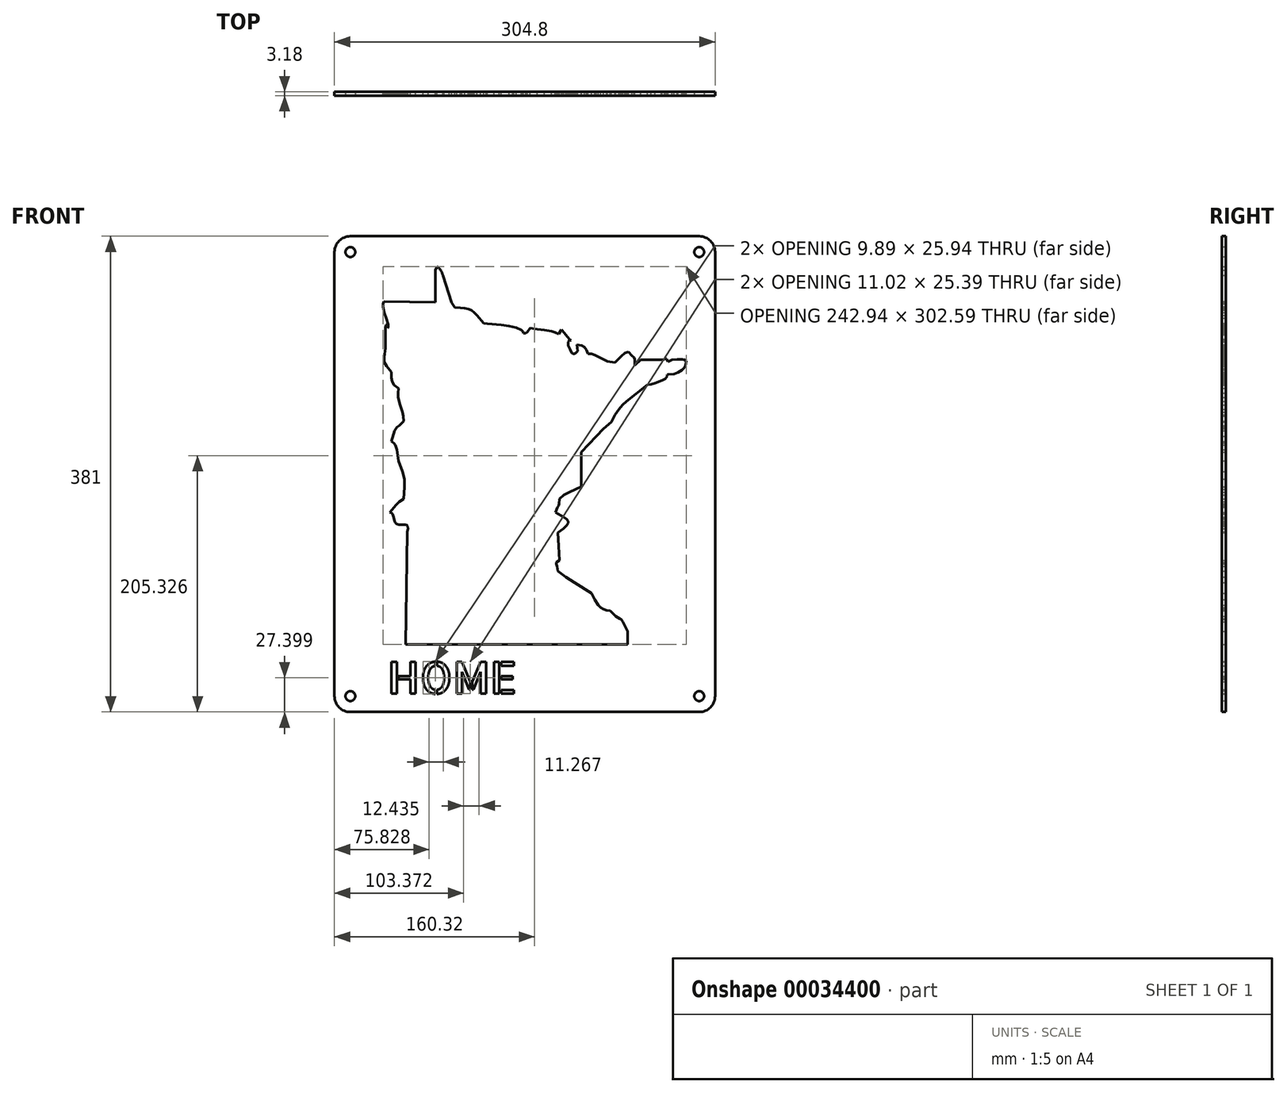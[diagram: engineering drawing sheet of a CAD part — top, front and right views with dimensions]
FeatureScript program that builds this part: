
annotation { "Feature Type Name" : "Feature", "Feature Type Description" : "" }
export const myFeature = defineFeature(function(context is Context, id is Id, definition is map)
    precondition{}
    {
        {
            var Q0;
            Q0=qCreatedBy(makeId("Front.planeOp"),FACE);
            var sketch = newSketch(context, id + "F0", { "sketchPlane" : qUnion([Q0])});
            skLineSegment(sketch, "E0", {"start": v(-79.4, 123.25) * mm, "end": v(-120.64, 123.97) * mm});
            skLineSegment(sketch, "E1", {"start": v(-120.64, 123.97) * mm, "end": v(-121.3, 121.8) * mm});
            skLineSegment(sketch, "E2", {"start": v(-121.3, 121.8) * mm, "end": v(-121.47, 119.63) * mm});
            skLineSegment(sketch, "E3", {"start": v(-121.47, 119.63) * mm, "end": v(-120.55, 115.04) * mm});
            skLineSegment(sketch, "E4", {"start": v(-120.55, 115.04) * mm, "end": v(-118.8, 110.36) * mm});
            skLineSegment(sketch, "E5", {"start": v(-118.8, 110.36) * mm, "end": v(-117.21, 105.52) * mm});
            skLineSegment(sketch, "E6", {"start": v(-117.21, 105.52) * mm, "end": v(-117.3, 102.76) * mm});
            skLineSegment(sketch, "E7", {"start": v(-117.3, 102.76) * mm, "end": v(-117.63, 102.51) * mm});
            skLineSegment(sketch, "E8", {"start": v(-117.63, 102.51) * mm, "end": v(-118.63, 104.85) * mm});
            skLineSegment(sketch, "E9", {"start": v(-118.63, 104.85) * mm, "end": v(-118.88, 105.18) * mm});
            skLineSegment(sketch, "E10", {"start": v(-118.88, 105.18) * mm, "end": v(-119.13, 105.02) * mm});
            skLineSegment(sketch, "E11", {"start": v(-119.13, 105.02) * mm, "end": v(-119.47, 102.84) * mm});
            skLineSegment(sketch, "E12", {"start": v(-119.47, 102.84) * mm, "end": v(-119.55, 86.3) * mm});
            skLineSegment(sketch, "E13", {"start": v(-119.55, 86.3) * mm, "end": v(-120.47, 79.38) * mm});
            skLineSegment(sketch, "E14", {"start": v(-120.47, 79.38) * mm, "end": v(-120.47, 75.28) * mm});
            skLineSegment(sketch, "E15", {"start": v(-120.47, 75.28) * mm, "end": v(-118.71, 72.03) * mm});
            skLineSegment(sketch, "E16", {"start": v(-118.71, 72.03) * mm, "end": v(-114.87, 67.18) * mm});
            skLineSegment(sketch, "E17", {"start": v(-114.87, 67.18) * mm, "end": v(-114.79, 62.84) * mm});
            skLineSegment(sketch, "E18", {"start": v(-114.79, 62.84) * mm, "end": v(-114.2, 59.58) * mm});
            skLineSegment(sketch, "E19", {"start": v(-114.2, 59.58) * mm, "end": v(-112.45, 56.91) * mm});
            skLineSegment(sketch, "E20", {"start": v(-112.45, 56.91) * mm, "end": v(-109.03, 54.4) * mm});
            skLineSegment(sketch, "E21", {"start": v(-109.03, 54.4) * mm, "end": v(-109.44, 50.56) * mm});
            skLineSegment(sketch, "E22", {"start": v(-109.44, 50.56) * mm, "end": v(-109.28, 47.14) * mm});
            skLineSegment(sketch, "E23", {"start": v(-109.28, 47.14) * mm, "end": v(-107.77, 41.13) * mm});
            skLineSegment(sketch, "E24", {"start": v(-107.77, 41.13) * mm, "end": v(-105.77, 35.28) * mm});
            skLineSegment(sketch, "E25", {"start": v(-105.77, 35.28) * mm, "end": v(-105.1, 31.94) * mm});
            skLineSegment(sketch, "E26", {"start": v(-105.1, 31.94) * mm, "end": v(-104.85, 28.1) * mm});
            skLineSegment(sketch, "E27", {"start": v(-104.85, 28.1) * mm, "end": v(-108.53, 24.6) * mm});
            skLineSegment(sketch, "E28", {"start": v(-108.53, 24.6) * mm, "end": v(-110.45, 23.34) * mm});
            skLineSegment(sketch, "E29", {"start": v(-110.45, 23.34) * mm, "end": v(-112.12, 20.5) * mm});
            skLineSegment(sketch, "E30", {"start": v(-112.12, 20.5) * mm, "end": v(-114.87, 11.81) * mm});
            skLineSegment(sketch, "E31", {"start": v(-114.87, 11.81) * mm, "end": v(-112.95, 10.65) * mm});
            skLineSegment(sketch, "E32", {"start": v(-112.95, 10.65) * mm, "end": v(-111.7, 9.06) * mm});
            skLineSegment(sketch, "E33", {"start": v(-111.7, 9.06) * mm, "end": v(-110.36, 5.22) * mm});
            skLineSegment(sketch, "E34", {"start": v(-110.36, 5.22) * mm, "end": v(-109.03, -3.89) * mm});
            skLineSegment(sketch, "E35", {"start": v(-109.03, -3.89) * mm, "end": v(-105.77, -12.24) * mm});
            skLineSegment(sketch, "E36", {"start": v(-105.77, -12.24) * mm, "end": v(-104.35, -18.25) * mm});
            skLineSegment(sketch, "E37", {"start": v(-104.35, -18.25) * mm, "end": v(-104.18, -24.6) * mm});
            skLineSegment(sketch, "E38", {"start": v(-104.18, -24.6) * mm, "end": v(-104.85, -34.37) * mm});
            skLineSegment(sketch, "E39", {"start": v(-104.85, -34.37) * mm, "end": v(-108.28, -36.62) * mm});
            skLineSegment(sketch, "E40", {"start": v(-108.28, -36.62) * mm, "end": v(-111.03, -38.96) * mm});
            skLineSegment(sketch, "E41", {"start": v(-111.03, -38.96) * mm, "end": v(-116.04, -45.06) * mm});
            skLineSegment(sketch, "E42", {"start": v(-116.04, -45.06) * mm, "end": v(-114.7, -45.4) * mm});
            skLineSegment(sketch, "E43", {"start": v(-114.7, -45.4) * mm, "end": v(-113.87, -46.31) * mm});
            skLineSegment(sketch, "E44", {"start": v(-113.87, -46.31) * mm, "end": v(-112.95, -49.15) * mm});
            skLineSegment(sketch, "E45", {"start": v(-112.95, -49.15) * mm, "end": v(-112.2, -52.16) * mm});
            skLineSegment(sketch, "E46", {"start": v(-112.2, -52.16) * mm, "end": v(-111.62, -53.4) * mm});
            skLineSegment(sketch, "E47", {"start": v(-111.62, -53.4) * mm, "end": v(-110.78, -54.24) * mm});
            skLineSegment(sketch, "E48", {"start": v(-110.78, -54.24) * mm, "end": v(-108.78, -54.75) * mm});
            skLineSegment(sketch, "E49", {"start": v(-108.78, -54.75) * mm, "end": v(-106.86, -54.91) * mm});
            skLineSegment(sketch, "E50", {"start": v(-106.86, -54.91) * mm, "end": v(-103.68, -55) * mm});
            skLineSegment(sketch, "E51", {"start": v(-103.68, -55) * mm, "end": v(-102.51, -55.33) * mm});
            skLineSegment(sketch, "E52", {"start": v(-102.51, -55.33) * mm, "end": v(-101.76, -56.25) * mm});
            skLineSegment(sketch, "E53", {"start": v(-101.76, -56.25) * mm, "end": v(-101.51, -57.92) * mm});
            skLineSegment(sketch, "E54", {"start": v(-101.51, -57.92) * mm, "end": v(-101.93, -60.68) * mm});
            skLineSegment(sketch, "E55", {"start": v(-101.93, -60.68) * mm, "end": v(-103.35, -150.79) * mm});
            skLineSegment(sketch, "E56", {"start": v(-103.35, -150.79) * mm, "end": v(74.45, -150.87) * mm});
            skLineSegment(sketch, "E57", {"start": v(74.45, -150.87) * mm, "end": v(74.45, -140.18) * mm});
            skLineSegment(sketch, "E58", {"start": v(74.45, -140.18) * mm, "end": v(70.7, -132.66) * mm});
            skLineSegment(sketch, "E59", {"start": v(70.7, -132.66) * mm, "end": v(69.36, -130.9) * mm});
            skLineSegment(sketch, "E60", {"start": v(69.36, -130.9) * mm, "end": v(68.02, -130) * mm});
            skLineSegment(sketch, "E61", {"start": v(68.02, -130) * mm, "end": v(65.02, -128.32) * mm});
            skLineSegment(sketch, "E62", {"start": v(65.02, -128.32) * mm, "end": v(60.34, -123.9) * mm});
            skLineSegment(sketch, "E63", {"start": v(60.34, -123.9) * mm, "end": v(57.5, -123.56) * mm});
            skLineSegment(sketch, "E64", {"start": v(57.5, -123.56) * mm, "end": v(55, -122.64) * mm});
            skLineSegment(sketch, "E65", {"start": v(55, -122.64) * mm, "end": v(52.82, -121.3) * mm});
            skLineSegment(sketch, "E66", {"start": v(52.82, -121.3) * mm, "end": v(50.98, -119.47) * mm});
            skLineSegment(sketch, "E67", {"start": v(50.98, -119.47) * mm, "end": v(48.06, -114.88) * mm});
            skLineSegment(sketch, "E68", {"start": v(48.06, -114.88) * mm, "end": v(45.64, -109.7) * mm});
            skLineSegment(sketch, "E69", {"start": v(45.64, -109.7) * mm, "end": v(31.78, -101.26) * mm});
            skLineSegment(sketch, "E70", {"start": v(31.78, -101.26) * mm, "end": v(24.85, -96.75) * mm});
            skLineSegment(sketch, "E71", {"start": v(24.85, -96.75) * mm, "end": v(18.58, -91.9) * mm});
            skLineSegment(sketch, "E72", {"start": v(18.58, -91.9) * mm, "end": v(18, -88.23) * mm});
            skLineSegment(sketch, "E73", {"start": v(18, -88.23) * mm, "end": v(17.16, -86.31) * mm});
            skLineSegment(sketch, "E74", {"start": v(17.16, -86.31) * mm, "end": v(17.33, -85.06) * mm});
            skLineSegment(sketch, "E75", {"start": v(17.33, -85.06) * mm, "end": v(19.75, -83.4) * mm});
            skLineSegment(sketch, "E76", {"start": v(19.75, -83.4) * mm, "end": v(19.17, -72.12) * mm});
            skLineSegment(sketch, "E77", {"start": v(19.17, -72.12) * mm, "end": v(18.58, -61.34) * mm});
            skLineSegment(sketch, "E78", {"start": v(18.58, -61.34) * mm, "end": v(23, -58) * mm});
            skLineSegment(sketch, "E79", {"start": v(23, -58) * mm, "end": v(25.68, -55.5) * mm});
            skLineSegment(sketch, "E80", {"start": v(25.68, -55.5) * mm, "end": v(26.85, -53.5) * mm});
            skLineSegment(sketch, "E81", {"start": v(26.85, -53.5) * mm, "end": v(26.68, -51.9) * mm});
            skLineSegment(sketch, "E82", {"start": v(26.68, -51.9) * mm, "end": v(25.43, -50.4) * mm});
            skLineSegment(sketch, "E83", {"start": v(25.43, -50.4) * mm, "end": v(23.26, -48.98) * mm});
            skLineSegment(sketch, "E84", {"start": v(23.26, -48.98) * mm, "end": v(16.83, -45.06) * mm});
            skLineSegment(sketch, "E85", {"start": v(16.83, -45.06) * mm, "end": v(18.25, -41.05) * mm});
            skLineSegment(sketch, "E86", {"start": v(18.25, -41.05) * mm, "end": v(19.08, -39.63) * mm});
            skLineSegment(sketch, "E87", {"start": v(19.08, -39.63) * mm, "end": v(19.58, -38.2) * mm});
            skLineSegment(sketch, "E88", {"start": v(19.58, -38.2) * mm, "end": v(19.75, -34.37) * mm});
            skLineSegment(sketch, "E89", {"start": v(19.75, -34.37) * mm, "end": v(23.34, -31.2) * mm});
            skLineSegment(sketch, "E90", {"start": v(23.34, -31.2) * mm, "end": v(27.85, -28.86) * mm});
            skLineSegment(sketch, "E91", {"start": v(27.85, -28.86) * mm, "end": v(32.7, -26.77) * mm});
            skLineSegment(sketch, "E92", {"start": v(32.7, -26.77) * mm, "end": v(37.37, -24.43) * mm});
            skLineSegment(sketch, "E93", {"start": v(37.37, -24.43) * mm, "end": v(37.37, 3.3) * mm});
            skLineSegment(sketch, "E94", {"start": v(37.37, 3.3) * mm, "end": v(49.23, 16) * mm});
            skLineSegment(sketch, "E95", {"start": v(49.23, 16) * mm, "end": v(55.24, 22) * mm});
            skLineSegment(sketch, "E96", {"start": v(55.24, 22) * mm, "end": v(61.5, 27.43) * mm});
            skLineSegment(sketch, "E97", {"start": v(61.5, 27.43) * mm, "end": v(64.43, 33.03) * mm});
            skLineSegment(sketch, "E98", {"start": v(64.43, 33.03) * mm, "end": v(67.35, 37.37) * mm});
            skLineSegment(sketch, "E99", {"start": v(67.35, 37.37) * mm, "end": v(70.28, 40.88) * mm});
            skLineSegment(sketch, "E100", {"start": v(70.28, 40.88) * mm, "end": v(73.45, 43.88) * mm});
            skLineSegment(sketch, "E101", {"start": v(73.45, 43.88) * mm, "end": v(90.32, 57.25) * mm});
            skLineSegment(sketch, "E102", {"start": v(90.32, 57.25) * mm, "end": v(93.24, 57.58) * mm});
            skLineSegment(sketch, "E103", {"start": v(93.24, 57.58) * mm, "end": v(96.42, 58.5) * mm});
            skLineSegment(sketch, "E104", {"start": v(96.42, 58.5) * mm, "end": v(102.01, 60.75) * mm});
            skLineSegment(sketch, "E105", {"start": v(102.01, 60.75) * mm, "end": v(104.52, 62) * mm});
            skLineSegment(sketch, "E106", {"start": v(104.52, 62) * mm, "end": v(105.69, 63.1) * mm});
            skLineSegment(sketch, "E107", {"start": v(105.69, 63.1) * mm, "end": v(106.1, 64.01) * mm});
            skLineSegment(sketch, "E108", {"start": v(106.1, 64.01) * mm, "end": v(106.02, 64.6) * mm});
            skLineSegment(sketch, "E109", {"start": v(106.02, 64.6) * mm, "end": v(106.1, 65.18) * mm});
            skLineSegment(sketch, "E110", {"start": v(106.1, 65.18) * mm, "end": v(106.69, 65.51) * mm});
            skLineSegment(sketch, "E111", {"start": v(106.69, 65.51) * mm, "end": v(111.45, 65.76) * mm});
            skLineSegment(sketch, "E112", {"start": v(111.45, 65.76) * mm, "end": v(114.7, 66.93) * mm});
            skLineSegment(sketch, "E113", {"start": v(114.7, 66.93) * mm, "end": v(117.96, 68.77) * mm});
            skLineSegment(sketch, "E114", {"start": v(117.96, 68.77) * mm, "end": v(119.38, 70.2) * mm});
            skLineSegment(sketch, "E115", {"start": v(119.38, 70.2) * mm, "end": v(120.47, 71.86) * mm});
            skLineSegment(sketch, "E116", {"start": v(120.47, 71.86) * mm, "end": v(121.22, 73.95) * mm});
            skLineSegment(sketch, "E117", {"start": v(121.22, 73.95) * mm, "end": v(121.47, 76.37) * mm});
            skLineSegment(sketch, "E118", {"start": v(121.47, 76.37) * mm, "end": v(119.97, 77.04) * mm});
            skLineSegment(sketch, "E119", {"start": v(119.97, 77.04) * mm, "end": v(118.21, 77.46) * mm});
            skLineSegment(sketch, "E120", {"start": v(118.21, 77.46) * mm, "end": v(114.12, 77.62) * mm});
            skLineSegment(sketch, "E121", {"start": v(114.12, 77.62) * mm, "end": v(110.11, 77.04) * mm});
            skLineSegment(sketch, "E122", {"start": v(110.11, 77.04) * mm, "end": v(106.77, 75.7) * mm});
            skLineSegment(sketch, "E123", {"start": v(106.77, 75.7) * mm, "end": v(105.6, 77.96) * mm});
            skLineSegment(sketch, "E124", {"start": v(105.6, 77.96) * mm, "end": v(105.02, 78.2) * mm});
            skLineSegment(sketch, "E125", {"start": v(105.02, 78.2) * mm, "end": v(103.93, 77.54) * mm});
            skLineSegment(sketch, "E126", {"start": v(103.93, 77.54) * mm, "end": v(101.43, 77.12) * mm});
            skLineSegment(sketch, "E127", {"start": v(101.43, 77.12) * mm, "end": v(84.97, 77.12) * mm});
            skLineSegment(sketch, "E128", {"start": v(84.97, 77.12) * mm, "end": v(80.3, 72.86) * mm});
            skLineSegment(sketch, "E129", {"start": v(80.3, 72.86) * mm, "end": v(80.21, 77.37) * mm});
            skLineSegment(sketch, "E130", {"start": v(80.21, 77.37) * mm, "end": v(79.63, 79.2) * mm});
            skLineSegment(sketch, "E131", {"start": v(79.63, 79.2) * mm, "end": v(78.04, 80.46) * mm});
            skLineSegment(sketch, "E132", {"start": v(78.04, 80.46) * mm, "end": v(75.04, 83.47) * mm});
            skLineSegment(sketch, "E133", {"start": v(75.04, 83.47) * mm, "end": v(72.36, 82.47) * mm});
            skLineSegment(sketch, "E134", {"start": v(72.36, 82.47) * mm, "end": v(69.27, 80.04) * mm});
            skLineSegment(sketch, "E135", {"start": v(69.27, 80.04) * mm, "end": v(64.43, 74.95) * mm});
            skLineSegment(sketch, "E136", {"start": v(64.43, 74.95) * mm, "end": v(58.33, 76.04) * mm});
            skLineSegment(sketch, "E137", {"start": v(58.33, 76.04) * mm, "end": v(53.16, 78.54) * mm});
            skLineSegment(sketch, "E138", {"start": v(53.16, 78.54) * mm, "end": v(48.23, 80.96) * mm});
            skLineSegment(sketch, "E139", {"start": v(48.23, 80.96) * mm, "end": v(45.56, 81.8) * mm});
            skLineSegment(sketch, "E140", {"start": v(45.56, 81.8) * mm, "end": v(42.63, 82.05) * mm});
            skLineSegment(sketch, "E141", {"start": v(42.63, 82.05) * mm, "end": v(41.46, 85.14) * mm});
            skLineSegment(sketch, "E142", {"start": v(41.46, 85.14) * mm, "end": v(39.88, 87.4) * mm});
            skLineSegment(sketch, "E143", {"start": v(39.88, 87.4) * mm, "end": v(37.54, 88.73) * mm});
            skLineSegment(sketch, "E144", {"start": v(37.54, 88.73) * mm, "end": v(33.86, 89.15) * mm});
            skLineSegment(sketch, "E145", {"start": v(33.86, 89.15) * mm, "end": v(34.45, 84.22) * mm});
            skLineSegment(sketch, "E146", {"start": v(34.45, 84.22) * mm, "end": v(32.86, 82.55) * mm});
            skLineSegment(sketch, "E147", {"start": v(32.86, 82.55) * mm, "end": v(31.6, 81.8) * mm});
            skLineSegment(sketch, "E148", {"start": v(31.6, 81.8) * mm, "end": v(30.6, 81.88) * mm});
            skLineSegment(sketch, "E149", {"start": v(30.6, 81.88) * mm, "end": v(29.77, 82.63) * mm});
            skLineSegment(sketch, "E150", {"start": v(29.77, 82.63) * mm, "end": v(28.44, 85.39) * mm});
            skLineSegment(sketch, "E151", {"start": v(28.44, 85.39) * mm, "end": v(26.77, 88.48) * mm});
            skLineSegment(sketch, "E152", {"start": v(26.77, 88.48) * mm, "end": v(26.93, 91.32) * mm});
            skLineSegment(sketch, "E153", {"start": v(26.93, 91.32) * mm, "end": v(27.6, 92.32) * mm});
            skLineSegment(sketch, "E154", {"start": v(27.6, 92.32) * mm, "end": v(29.19, 92.74) * mm});
            skLineSegment(sketch, "E155", {"start": v(29.19, 92.74) * mm, "end": v(27.77, 93.74) * mm});
            skLineSegment(sketch, "E156", {"start": v(27.77, 93.74) * mm, "end": v(24.85, 97.17) * mm});
            skLineSegment(sketch, "E157", {"start": v(24.85, 97.17) * mm, "end": v(22.17, 100.59) * mm});
            skLineSegment(sketch, "E158", {"start": v(22.17, 100.59) * mm, "end": v(21.5, 101.42) * mm});
            skLineSegment(sketch, "E159", {"start": v(21.5, 101.42) * mm, "end": v(21.5, 101.26) * mm});
            skLineSegment(sketch, "E160", {"start": v(21.5, 101.26) * mm, "end": v(19.17, 97.75) * mm});
            skLineSegment(sketch, "E161", {"start": v(19.17, 97.75) * mm, "end": v(16.33, 99.09) * mm});
            skLineSegment(sketch, "E162", {"start": v(16.33, 99.09) * mm, "end": v(13.4, 100) * mm});
            skLineSegment(sketch, "E163", {"start": v(13.4, 100) * mm, "end": v(7.72, 100.92) * mm});
            skLineSegment(sketch, "E164", {"start": v(7.72, 100.92) * mm, "end": v(2.05, 101.5) * mm});
            skLineSegment(sketch, "E165", {"start": v(2.05, 101.5) * mm, "end": v(-3.8, 102.68) * mm});
            skLineSegment(sketch, "E166", {"start": v(-3.8, 102.68) * mm, "end": v(-5.8, 99.25) * mm});
            skLineSegment(sketch, "E167", {"start": v(-5.8, 99.25) * mm, "end": v(-7.14, 98.58) * mm});
            skLineSegment(sketch, "E168", {"start": v(-7.14, 98.58) * mm, "end": v(-9.06, 98.42) * mm});
            skLineSegment(sketch, "E169", {"start": v(-9.06, 98.42) * mm, "end": v(-9.48, 99.84) * mm});
            skLineSegment(sketch, "E170", {"start": v(-9.48, 99.84) * mm, "end": v(-10.56, 100.92) * mm});
            skLineSegment(sketch, "E171", {"start": v(-10.56, 100.92) * mm, "end": v(-14.66, 102.84) * mm});
            skLineSegment(sketch, "E172", {"start": v(-14.66, 102.84) * mm, "end": v(-20.34, 104.26) * mm});
            skLineSegment(sketch, "E173", {"start": v(-20.34, 104.26) * mm, "end": v(-26.68, 105.18) * mm});
            skLineSegment(sketch, "E174", {"start": v(-26.68, 105.18) * mm, "end": v(-37.79, 106.18) * mm});
            skLineSegment(sketch, "E175", {"start": v(-37.79, 106.18) * mm, "end": v(-40.8, 106.35) * mm});
            skLineSegment(sketch, "E176", {"start": v(-40.8, 106.35) * mm, "end": v(-41.21, 106.35) * mm});
            skLineSegment(sketch, "E177", {"start": v(-41.21, 106.35) * mm, "end": v(-40.8, 106.27) * mm});
            skLineSegment(sketch, "E178", {"start": v(-40.8, 106.27) * mm, "end": v(-46.22, 112.87) * mm});
            skLineSegment(sketch, "E179", {"start": v(-46.22, 112.87) * mm, "end": v(-48.48, 115.12) * mm});
            skLineSegment(sketch, "E180", {"start": v(-48.48, 115.12) * mm, "end": v(-50.73, 116.8) * mm});
            skLineSegment(sketch, "E181", {"start": v(-50.73, 116.8) * mm, "end": v(-53.16, 117.88) * mm});
            skLineSegment(sketch, "E182", {"start": v(-53.16, 117.88) * mm, "end": v(-56, 118.46) * mm});
            skLineSegment(sketch, "E183", {"start": v(-56, 118.46) * mm, "end": v(-59.42, 118.63) * mm});
            skLineSegment(sketch, "E184", {"start": v(-59.42, 118.63) * mm, "end": v(-63.87, 119.13) * mm});
            skLineSegment(sketch, "E185", {"start": v(-63.87, 119.13) * mm, "end": v(-66.57, 123.02) * mm});
            skLineSegment(sketch, "E186", {"start": v(-66.57, 123.02) * mm, "end": v(-73.57, 144.67) * mm});
            skLineSegment(sketch, "E187", {"start": v(-78.2, 151.72) * mm, "end": v(-79.63, 148.92) * mm});
            skLineSegment(sketch, "E188", {"start": v(-79.63, 148.92) * mm, "end": v(-79.4, 123.25) * mm});
            skArc(sketch, "E189", {"start": v(-73.57, 144.67) * mm, "mid": v(-75.15, 148.67) * mm, "end": v(-78.2, 151.72) * mm});
            skPoint(sketch, "E190.orphan", {"position": v(-76.76, 154.52) * mm});
            skSolve(sketch);
        }
        {
            var Q0;
            Q0=makeQuery(id+"F0.imprint","IMPRINT",FACE,{"disambiguationData":[TD([[makeQuery(id+"F0.imprint","IMPRINT",EDGE,{"derivedFrom":sQuery(id+"F0.wireOp",EDGE,"E0")}),1.0]])]});
            var sketch = newSketch(context, id + "F1", { "sketchPlane" : qUnion([Q0])});
            skLineSegment(sketch, "E191.bottom", {"start": v(-147.62, 176.1) * mm, "end": v(131.78, 176.1) * mm});
            skLineSegment(sketch, "E191.top", {"start": v(-147.62, -204.9) * mm, "end": v(131.78, -204.9) * mm});
            skLineSegment(sketch, "E191.left", {"start": v(-160.32, 163.4) * mm, "end": v(-160.32, -192.2) * mm});
            skLineSegment(sketch, "E191.right", {"start": v(144.48, 163.4) * mm, "end": v(144.48, -192.2) * mm});
            skPoint(sketch, "E192.visualSharp", {"position": v(144.48, 176.1) * mm});
            skArc(sketch, "E192.filletArc", {"start": v(144.48, 163.4) * mm, "mid": v(140.76, 172.38) * mm, "end": v(131.78, 176.1) * mm});
            skPoint(sketch, "E193.visualSharp", {"position": v(144.48, -204.9) * mm});
            skArc(sketch, "E193.filletArc", {"start": v(131.78, -204.9) * mm, "mid": v(140.76, -201.18) * mm, "end": v(144.48, -192.2) * mm});
            skPoint(sketch, "E194.visualSharp", {"position": v(-160.32, -204.9) * mm});
            skArc(sketch, "E194.filletArc", {"start": v(-160.32, -192.2) * mm, "mid": v(-156.6, -201.18) * mm, "end": v(-147.62, -204.9) * mm});
            skPoint(sketch, "E195.visualSharp", {"position": v(-160.32, 176.1) * mm});
            skArc(sketch, "E195.filletArc", {"start": v(-147.62, 176.1) * mm, "mid": v(-156.6, 172.38) * mm, "end": v(-160.32, 163.4) * mm});
            skText(sketch, "E196", { "text": "HOME\n\n", "fontName": "AllertaStencil-Regular.ttf"});
            const initialGuessF1  = {"E196": [-0.11789, -0.1903, 1, 0, 0.0254]};
            skSetInitialGuess(sketch, initialGuessF1);
            skSolve(sketch);
        }
        {
            var Q0;
            Q0=makeQuery(id+"F1.imprint","IMPRINT",FACE,{"disambiguationData":[TD([[makeQuery(id+"F1.imprint","IMPRINT",EDGE,{"derivedFrom":sQuery(id+"F1.wireOp",EDGE,"E191.bottom")}),-1.0]])]});
            extrude(context, id + "F2", {"entities" : qUnion([Q0]), "depth" : 3.17 * mm});
        }
        {
            var Q0;
            Q0=makeQuery(id+"F2.opExtrude","CAP_FACE",FACE,{"disambiguationData":[OSD([sQuery(id+"F0.wireOp",EDGE,"E0"),sQuery(id+"F0.wireOp",EDGE,"E1"),sQuery(id+"F0.wireOp",EDGE,"E2"),sQuery(id+"F0.wireOp",EDGE,"E3"),sQuery(id+"F0.wireOp",EDGE,"E4"),sQuery(id+"F0.wireOp",EDGE,"E5"),sQuery(id+"F0.wireOp",EDGE,"E6"),sQuery(id+"F0.wireOp",EDGE,"E7"),sQuery(id+"F0.wireOp",EDGE,"E8"),sQuery(id+"F0.wireOp",EDGE,"E9"),sQuery(id+"F0.wireOp",EDGE,"E10"),sQuery(id+"F0.wireOp",EDGE,"E11"),sQuery(id+"F0.wireOp",EDGE,"E12"),sQuery(id+"F0.wireOp",EDGE,"E13"),sQuery(id+"F0.wireOp",EDGE,"E14"),sQuery(id+"F0.wireOp",EDGE,"E15"),sQuery(id+"F0.wireOp",EDGE,"E16"),sQuery(id+"F0.wireOp",EDGE,"E17"),sQuery(id+"F0.wireOp",EDGE,"E18"),sQuery(id+"F0.wireOp",EDGE,"E19"),sQuery(id+"F0.wireOp",EDGE,"E20"),sQuery(id+"F0.wireOp",EDGE,"E21"),sQuery(id+"F0.wireOp",EDGE,"E22"),sQuery(id+"F0.wireOp",EDGE,"E23"),sQuery(id+"F0.wireOp",EDGE,"E24"),sQuery(id+"F0.wireOp",EDGE,"E25"),sQuery(id+"F0.wireOp",EDGE,"E26"),sQuery(id+"F0.wireOp",EDGE,"E27"),sQuery(id+"F0.wireOp",EDGE,"E28"),sQuery(id+"F0.wireOp",EDGE,"E29"),sQuery(id+"F0.wireOp",EDGE,"E30"),sQuery(id+"F0.wireOp",EDGE,"E31"),sQuery(id+"F0.wireOp",EDGE,"E32"),sQuery(id+"F0.wireOp",EDGE,"E33"),sQuery(id+"F0.wireOp",EDGE,"E34"),sQuery(id+"F0.wireOp",EDGE,"E35"),sQuery(id+"F0.wireOp",EDGE,"E36"),sQuery(id+"F0.wireOp",EDGE,"E37"),sQuery(id+"F0.wireOp",EDGE,"E38"),sQuery(id+"F0.wireOp",EDGE,"E39"),sQuery(id+"F0.wireOp",EDGE,"E40"),sQuery(id+"F0.wireOp",EDGE,"E41"),sQuery(id+"F0.wireOp",EDGE,"E42"),sQuery(id+"F0.wireOp",EDGE,"E43"),sQuery(id+"F0.wireOp",EDGE,"E44"),sQuery(id+"F0.wireOp",EDGE,"E45"),sQuery(id+"F0.wireOp",EDGE,"E46"),sQuery(id+"F0.wireOp",EDGE,"E47"),sQuery(id+"F0.wireOp",EDGE,"E48"),sQuery(id+"F0.wireOp",EDGE,"E49"),sQuery(id+"F0.wireOp",EDGE,"E50"),sQuery(id+"F0.wireOp",EDGE,"E51"),sQuery(id+"F0.wireOp",EDGE,"E52"),sQuery(id+"F0.wireOp",EDGE,"E53"),sQuery(id+"F0.wireOp",EDGE,"E54"),sQuery(id+"F0.wireOp",EDGE,"E55"),sQuery(id+"F0.wireOp",EDGE,"E56"),sQuery(id+"F0.wireOp",EDGE,"E57"),sQuery(id+"F0.wireOp",EDGE,"E58"),sQuery(id+"F0.wireOp",EDGE,"E59"),sQuery(id+"F0.wireOp",EDGE,"E60"),sQuery(id+"F0.wireOp",EDGE,"E61"),sQuery(id+"F0.wireOp",EDGE,"E62"),sQuery(id+"F0.wireOp",EDGE,"E63"),sQuery(id+"F0.wireOp",EDGE,"E64"),sQuery(id+"F0.wireOp",EDGE,"E65"),sQuery(id+"F0.wireOp",EDGE,"E66"),sQuery(id+"F0.wireOp",EDGE,"E67"),sQuery(id+"F0.wireOp",EDGE,"E68"),sQuery(id+"F0.wireOp",EDGE,"E69"),sQuery(id+"F0.wireOp",EDGE,"E70"),sQuery(id+"F0.wireOp",EDGE,"E71"),sQuery(id+"F0.wireOp",EDGE,"E72"),sQuery(id+"F0.wireOp",EDGE,"E73"),sQuery(id+"F0.wireOp",EDGE,"E74"),sQuery(id+"F0.wireOp",EDGE,"E75"),sQuery(id+"F0.wireOp",EDGE,"E76"),sQuery(id+"F0.wireOp",EDGE,"E77"),sQuery(id+"F0.wireOp",EDGE,"E78"),sQuery(id+"F0.wireOp",EDGE,"E79"),sQuery(id+"F0.wireOp",EDGE,"E80"),sQuery(id+"F0.wireOp",EDGE,"E81"),sQuery(id+"F0.wireOp",EDGE,"E82"),sQuery(id+"F0.wireOp",EDGE,"E83"),sQuery(id+"F0.wireOp",EDGE,"E84"),sQuery(id+"F0.wireOp",EDGE,"E85"),sQuery(id+"F0.wireOp",EDGE,"E86"),sQuery(id+"F0.wireOp",EDGE,"E87"),sQuery(id+"F0.wireOp",EDGE,"E88"),sQuery(id+"F0.wireOp",EDGE,"E89"),sQuery(id+"F0.wireOp",EDGE,"E90"),sQuery(id+"F0.wireOp",EDGE,"E91"),sQuery(id+"F0.wireOp",EDGE,"E92"),sQuery(id+"F0.wireOp",EDGE,"E93"),sQuery(id+"F0.wireOp",EDGE,"E94"),sQuery(id+"F0.wireOp",EDGE,"E95"),sQuery(id+"F0.wireOp",EDGE,"E96"),sQuery(id+"F0.wireOp",EDGE,"E97"),sQuery(id+"F0.wireOp",EDGE,"E98"),sQuery(id+"F0.wireOp",EDGE,"E99"),sQuery(id+"F0.wireOp",EDGE,"E100"),sQuery(id+"F0.wireOp",EDGE,"E101"),sQuery(id+"F0.wireOp",EDGE,"E102"),sQuery(id+"F0.wireOp",EDGE,"E103"),sQuery(id+"F0.wireOp",EDGE,"E104"),sQuery(id+"F0.wireOp",EDGE,"E105"),sQuery(id+"F0.wireOp",EDGE,"E106"),sQuery(id+"F0.wireOp",EDGE,"E107"),sQuery(id+"F0.wireOp",EDGE,"E108"),sQuery(id+"F0.wireOp",EDGE,"E109"),sQuery(id+"F0.wireOp",EDGE,"E110"),sQuery(id+"F0.wireOp",EDGE,"E111"),sQuery(id+"F0.wireOp",EDGE,"E112"),sQuery(id+"F0.wireOp",EDGE,"E113"),sQuery(id+"F0.wireOp",EDGE,"E114"),sQuery(id+"F0.wireOp",EDGE,"E115"),sQuery(id+"F0.wireOp",EDGE,"E116"),sQuery(id+"F0.wireOp",EDGE,"E117"),sQuery(id+"F0.wireOp",EDGE,"E118"),sQuery(id+"F0.wireOp",EDGE,"E119"),sQuery(id+"F0.wireOp",EDGE,"E120"),sQuery(id+"F0.wireOp",EDGE,"E121"),sQuery(id+"F0.wireOp",EDGE,"E122"),sQuery(id+"F0.wireOp",EDGE,"E123"),sQuery(id+"F0.wireOp",EDGE,"E124"),sQuery(id+"F0.wireOp",EDGE,"E125"),sQuery(id+"F0.wireOp",EDGE,"E126"),sQuery(id+"F0.wireOp",EDGE,"E127"),sQuery(id+"F0.wireOp",EDGE,"E128"),sQuery(id+"F0.wireOp",EDGE,"E129"),sQuery(id+"F0.wireOp",EDGE,"E130"),sQuery(id+"F0.wireOp",EDGE,"E131"),sQuery(id+"F0.wireOp",EDGE,"E132"),sQuery(id+"F0.wireOp",EDGE,"E133"),sQuery(id+"F0.wireOp",EDGE,"E134"),sQuery(id+"F0.wireOp",EDGE,"E135"),sQuery(id+"F0.wireOp",EDGE,"E136"),sQuery(id+"F0.wireOp",EDGE,"E137"),sQuery(id+"F0.wireOp",EDGE,"E138"),sQuery(id+"F0.wireOp",EDGE,"E139"),sQuery(id+"F0.wireOp",EDGE,"E140"),sQuery(id+"F0.wireOp",EDGE,"E141"),sQuery(id+"F0.wireOp",EDGE,"E142"),sQuery(id+"F0.wireOp",EDGE,"E143"),sQuery(id+"F0.wireOp",EDGE,"E144"),sQuery(id+"F0.wireOp",EDGE,"E145"),sQuery(id+"F0.wireOp",EDGE,"E146"),sQuery(id+"F0.wireOp",EDGE,"E147"),sQuery(id+"F0.wireOp",EDGE,"E148"),sQuery(id+"F0.wireOp",EDGE,"E149"),sQuery(id+"F0.wireOp",EDGE,"E150"),sQuery(id+"F0.wireOp",EDGE,"E151"),sQuery(id+"F0.wireOp",EDGE,"E152"),sQuery(id+"F0.wireOp",EDGE,"E153"),sQuery(id+"F0.wireOp",EDGE,"E154"),sQuery(id+"F0.wireOp",EDGE,"E155"),sQuery(id+"F0.wireOp",EDGE,"E156"),sQuery(id+"F0.wireOp",EDGE,"E157"),sQuery(id+"F0.wireOp",EDGE,"E158"),sQuery(id+"F0.wireOp",EDGE,"E159"),sQuery(id+"F0.wireOp",EDGE,"E160"),sQuery(id+"F0.wireOp",EDGE,"E161"),sQuery(id+"F0.wireOp",EDGE,"E162"),sQuery(id+"F0.wireOp",EDGE,"E163"),sQuery(id+"F0.wireOp",EDGE,"E164"),sQuery(id+"F0.wireOp",EDGE,"E165"),sQuery(id+"F0.wireOp",EDGE,"E166"),sQuery(id+"F0.wireOp",EDGE,"E167"),sQuery(id+"F0.wireOp",EDGE,"E168"),sQuery(id+"F0.wireOp",EDGE,"E169"),sQuery(id+"F0.wireOp",EDGE,"E170"),sQuery(id+"F0.wireOp",EDGE,"E171"),sQuery(id+"F0.wireOp",EDGE,"E172"),sQuery(id+"F0.wireOp",EDGE,"E173"),sQuery(id+"F0.wireOp",EDGE,"E174"),sQuery(id+"F0.wireOp",EDGE,"E175"),sQuery(id+"F0.wireOp",EDGE,"E176"),sQuery(id+"F0.wireOp",EDGE,"E178"),sQuery(id+"F0.wireOp",EDGE,"E179"),sQuery(id+"F0.wireOp",EDGE,"E180"),sQuery(id+"F0.wireOp",EDGE,"E181"),sQuery(id+"F0.wireOp",EDGE,"E182"),sQuery(id+"F0.wireOp",EDGE,"E183"),sQuery(id+"F0.wireOp",EDGE,"E184"),sQuery(id+"F0.wireOp",EDGE,"E185"),sQuery(id+"F0.wireOp",EDGE,"E186"),sQuery(id+"F0.wireOp",EDGE,"E187"),sQuery(id+"F0.wireOp",EDGE,"E188"),sQuery(id+"F1.wireOp",EDGE,"E191.bottom"),sQuery(id+"F1.wireOp",EDGE,"E191.top"),sQuery(id+"F1.wireOp",EDGE,"E191.left"),sQuery(id+"F1.wireOp",EDGE,"E191.right"),sQuery(id+"F1.wireOp",EDGE,"E192.filletArc"),sQuery(id+"F1.wireOp",EDGE,"E193.filletArc"),sQuery(id+"F1.wireOp",EDGE,"E194.filletArc"),sQuery(id+"F1.wireOp",EDGE,"E195.filletArc"),sQuery(id+"F1.wireOp",EDGE,"E196.sketch_text.stroke-0"),sQuery(id+"F1.wireOp",EDGE,"E196.sketch_text.stroke-1"),sQuery(id+"F1.wireOp",EDGE,"E196.sketch_text.stroke-2"),sQuery(id+"F1.wireOp",EDGE,"E196.sketch_text.stroke-3"),sQuery(id+"F1.wireOp",EDGE,"E196.sketch_text.stroke-4"),sQuery(id+"F1.wireOp",EDGE,"E196.sketch_text.stroke-5"),sQuery(id+"F1.wireOp",EDGE,"E196.sketch_text.stroke-6"),sQuery(id+"F1.wireOp",EDGE,"E196.sketch_text.stroke-7"),sQuery(id+"F1.wireOp",EDGE,"E196.sketch_text.stroke-8"),sQuery(id+"F1.wireOp",EDGE,"E196.sketch_text.stroke-9"),sQuery(id+"F1.wireOp",EDGE,"E196.sketch_text.stroke-10"),sQuery(id+"F1.wireOp",EDGE,"E196.sketch_text.stroke-11"),sQuery(id+"F1.wireOp",EDGE,"E196.sketch_text.stroke-12"),sQuery(id+"F1.wireOp",EDGE,"E196.sketch_text.stroke-13"),sQuery(id+"F1.wireOp",EDGE,"E196.sketch_text.stroke-14"),sQuery(id+"F1.wireOp",EDGE,"E196.sketch_text.stroke-15"),sQuery(id+"F1.wireOp",EDGE,"E196.sketch_text.stroke-16"),sQuery(id+"F1.wireOp",EDGE,"E196.sketch_text.stroke-17"),sQuery(id+"F1.wireOp",EDGE,"E196.sketch_text.stroke-18"),sQuery(id+"F1.wireOp",EDGE,"E196.sketch_text.stroke-19"),sQuery(id+"F1.wireOp",EDGE,"E196.sketch_text.stroke-20"),sQuery(id+"F1.wireOp",EDGE,"E196.sketch_text.stroke-21"),sQuery(id+"F1.wireOp",EDGE,"E196.sketch_text.stroke-22"),sQuery(id+"F1.wireOp",EDGE,"E196.sketch_text.stroke-23"),sQuery(id+"F1.wireOp",EDGE,"E196.sketch_text.stroke-24"),sQuery(id+"F1.wireOp",EDGE,"E196.sketch_text.stroke-25"),sQuery(id+"F1.wireOp",EDGE,"E196.sketch_text.stroke-26"),sQuery(id+"F1.wireOp",EDGE,"E196.sketch_text.stroke-27"),sQuery(id+"F1.wireOp",EDGE,"E196.sketch_text.stroke-28"),sQuery(id+"F1.wireOp",EDGE,"E196.sketch_text.stroke-29"),sQuery(id+"F1.wireOp",EDGE,"E196.sketch_text.stroke-30"),sQuery(id+"F1.wireOp",EDGE,"E196.sketch_text.stroke-31"),sQuery(id+"F1.wireOp",EDGE,"E196.sketch_text.stroke-32"),sQuery(id+"F1.wireOp",EDGE,"E196.sketch_text.stroke-33"),sQuery(id+"F1.wireOp",EDGE,"E196.sketch_text.stroke-34"),sQuery(id+"F1.wireOp",EDGE,"E196.sketch_text.stroke-35"),sQuery(id+"F1.wireOp",EDGE,"E196.sketch_text.stroke-36"),sQuery(id+"F1.wireOp",EDGE,"E196.sketch_text.stroke-37"),sQuery(id+"F1.wireOp",EDGE,"E196.sketch_text.stroke-38"),sQuery(id+"F1.wireOp",EDGE,"E196.sketch_text.stroke-39"),sQuery(id+"F1.wireOp",EDGE,"E196.sketch_text.stroke-40"),sQuery(id+"F1.wireOp",EDGE,"E196.sketch_text.stroke-41"),sQuery(id+"F1.wireOp",EDGE,"E196.sketch_text.stroke-42"),sQuery(id+"F1.wireOp",EDGE,"E196.sketch_text.stroke-43"),sQuery(id+"F1.wireOp",EDGE,"E196.sketch_text.stroke-44"),sQuery(id+"F1.wireOp",EDGE,"E196.sketch_text.stroke-45"),sQuery(id+"F1.wireOp",EDGE,"E196.sketch_text.stroke-46"),sQuery(id+"F1.wireOp",EDGE,"E196.sketch_text.stroke-47"),sQuery(id+"F1.wireOp",EDGE,"E196.sketch_text.stroke-48"),sQuery(id+"F1.wireOp",EDGE,"E196.sketch_text.stroke-49"),sQuery(id+"F1.wireOp",EDGE,"E196.sketch_text.stroke-50"),sQuery(id+"F1.wireOp",EDGE,"E196.sketch_text.stroke-51"),sQuery(id+"F1.wireOp",EDGE,"E196.sketch_text.stroke-52"),sQuery(id+"F1.wireOp",EDGE,"E196.sketch_text.stroke-53"),sQuery(id+"F1.wireOp",EDGE,"E196.sketch_text.stroke-54"),sQuery(id+"F1.wireOp",EDGE,"E196.sketch_text.stroke-55"),sQuery(id+"F1.wireOp",EDGE,"E196.sketch_text.stroke-56"),sQuery(id+"F1.wireOp",EDGE,"E196.sketch_text.stroke-57"),sQuery(id+"F1.wireOp",EDGE,"E196.sketch_text.stroke-58"),sQuery(id+"F1.wireOp",EDGE,"E196.sketch_text.stroke-59"),sQuery(id+"F1.wireOp",EDGE,"E196.sketch_text.stroke-60"),sQuery(id+"F1.wireOp",EDGE,"E196.sketch_text.stroke-61"),sQuery(id+"F1.wireOp",EDGE,"E196.sketch_text.stroke-62"),sQuery(id+"F1.wireOp",EDGE,"E196.sketch_text.stroke-63"),sQuery(id+"F1.wireOp",EDGE,"E196.sketch_text.stroke-64"),sQuery(id+"F1.wireOp",EDGE,"E196.sketch_text.stroke-65"),sQuery(id+"F1.wireOp",EDGE,"E196.sketch_text.stroke-66"),sQuery(id+"F1.wireOp",EDGE,"E196.sketch_text.stroke-67"),sQuery(id+"F1.wireOp",EDGE,"E196.sketch_text.stroke-68"),sQuery(id+"F1.wireOp",EDGE,"E196.sketch_text.stroke-69"),sQuery(id+"F1.wireOp",EDGE,"E196.sketch_text.stroke-70"),sQuery(id+"F1.wireOp",EDGE,"E196.sketch_text.stroke-71"),sQuery(id+"F1.wireOp",EDGE,"E196.sketch_text.stroke-72"),sQuery(id+"F1.wireOp",EDGE,"E196.sketch_text.stroke-73"),sQuery(id+"F1.wireOp",EDGE,"E196.sketch_text.stroke-74"),sQuery(id+"F1.wireOp",EDGE,"E196.sketch_text.stroke-75"),sQuery(id+"F1.wireOp",EDGE,"E196.sketch_text.stroke-76"),sQuery(id+"F1.wireOp",EDGE,"E196.sketch_text.stroke-77"),sQuery(id+"F1.wireOp",EDGE,"E196.sketch_text.stroke-78"),sQuery(id+"F1.wireOp",EDGE,"E196.sketch_text.stroke-79"),sQuery(id+"F1.wireOp",EDGE,"E196.sketch_text.stroke-80"),sQuery(id+"F1.wireOp",EDGE,"E196.sketch_text.stroke-81"),sQuery(id+"F1.wireOp",EDGE,"E196.sketch_text.stroke-82"),sQuery(id+"F1.wireOp",EDGE,"E196.sketch_text.stroke-83"),sQuery(id+"F1.wireOp",EDGE,"E196.sketch_text.stroke-84"),sQuery(id+"F1.wireOp",EDGE,"E196.sketch_text.stroke-85"),sQuery(id+"F1.wireOp",EDGE,"E196.sketch_text.stroke-86"),sQuery(id+"F1.wireOp",EDGE,"E196.sketch_text.stroke-87"),sQuery(id+"F1.wireOp",EDGE,"E196.sketch_text.stroke-88"),sQuery(id+"F1.wireOp",EDGE,"E196.sketch_text.stroke-89"),sQuery(id+"F1.wireOp",EDGE,"E196.sketch_text.stroke-90"),sQuery(id+"F1.wireOp",EDGE,"E196.sketch_text.stroke-91"),sQuery(id+"F1.wireOp",EDGE,"E196.sketch_text.stroke-92"),sQuery(id+"F1.wireOp",EDGE,"E196.sketch_text.stroke-93"),sQuery(id+"F1.wireOp",EDGE,"E196.sketch_text.stroke-94"),sQuery(id+"F1.wireOp",EDGE,"E196.sketch_text.stroke-95"),sQuery(id+"F1.wireOp",EDGE,"E196.sketch_text.stroke-96"),sQuery(id+"F1.wireOp",EDGE,"E196.sketch_text.stroke-97"),sQuery(id+"F1.wireOp",EDGE,"E196.sketch_text.stroke-98"),sQuery(id+"F1.wireOp",EDGE,"E196.sketch_text.stroke-99"),sQuery(id+"F1.wireOp",EDGE,"E196.sketch_text.stroke-100"),sQuery(id+"F1.wireOp",EDGE,"E196.sketch_text.stroke-101"),sQuery(id+"F1.wireOp",EDGE,"E196.sketch_text.stroke-102"),sQuery(id+"F1.wireOp",EDGE,"E196.sketch_text.stroke-103"),sQuery(id+"F1.wireOp",EDGE,"E196.sketch_text.stroke-104"),sQuery(id+"F1.wireOp",EDGE,"E196.sketch_text.stroke-105"),sQuery(id+"F1.wireOp",EDGE,"E196.sketch_text.stroke-106"),sQuery(id+"F1.wireOp",EDGE,"E196.sketch_text.stroke-107"),sQuery(id+"F1.wireOp",EDGE,"E196.sketch_text.stroke-108"),sQuery(id+"F1.wireOp",EDGE,"E196.sketch_text.stroke-109"),sQuery(id+"F1.wireOp",EDGE,"E196.sketch_text.stroke-110"),sQuery(id+"F1.wireOp",EDGE,"E196.sketch_text.stroke-111"),sQuery(id+"F1.wireOp",EDGE,"E196.sketch_text.stroke-112"),sQuery(id+"F1.wireOp",EDGE,"E196.sketch_text.stroke-113"),sQuery(id+"F1.wireOp",EDGE,"E196.sketch_text.stroke-114"),sQuery(id+"F1.wireOp",EDGE,"E196.sketch_text.stroke-115"),sQuery(id+"F1.wireOp",EDGE,"E196.sketch_text.stroke-116"),sQuery(id+"F1.wireOp",EDGE,"E196.sketch_text.stroke-117"),sQuery(id+"F1.wireOp",EDGE,"E196.sketch_text.stroke-118"),sQuery(id+"F1.wireOp",EDGE,"E196.sketch_text.stroke-119")])],"isStart":false});
            var sketch = newSketch(context, id + "F3", { "sketchPlane" : qUnion([Q0])});
            skCircle(sketch, "E197", {"center": v(-147.62, 163.4) * mm, "radius": 3.98 * mm});
            skCircle(sketch, "E198", {"center": v(131.78, 163.4) * mm, "radius": 3.98 * mm});
            skCircle(sketch, "E199", {"center": v(131.78, -192.2) * mm, "radius": 3.98 * mm});
            skCircle(sketch, "E200", {"center": v(-147.62, -192.2) * mm, "radius": 3.98 * mm});
            skSolve(sketch);
        }
        {
            var Q0;
            Q0 = qSketchRegion(id + "F3", true);
            extrude(context, id + "F4", {"entities" : qUnion([Q0]), "operationType" : NewBodyOperationType.REMOVE, "oppositeDirection" : true, "depth" : 25.4 * mm});
        }
    });
